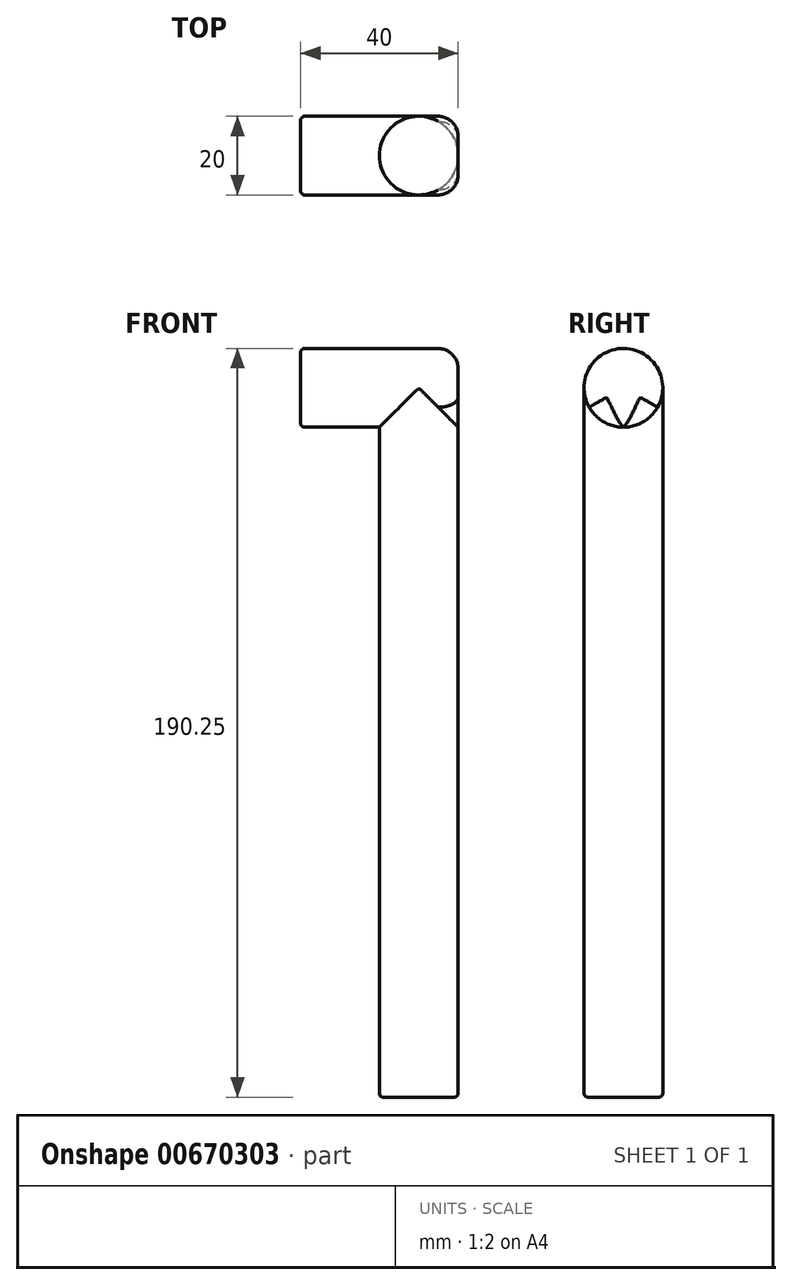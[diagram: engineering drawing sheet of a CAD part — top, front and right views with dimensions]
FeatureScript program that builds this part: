
annotation { "Feature Type Name" : "Feature", "Feature Type Description" : "" }
export const myFeature = defineFeature(function(context is Context, id is Id, definition is map)
    precondition{}
    {
        {
            var Q0;
            Q0=qCreatedBy(makeId("Top.planeOp"),FACE);
            var sketch = newSketch(context, id + "F0", { "sketchPlane" : qUnion([Q0])});
            skCircle(sketch, "E0", {"center": v(0, 0) * mm, "radius": 10 * mm});
            skSolve(sketch);
        }
        {
            var Q0;
            Q0=qCreatedBy(makeId("Right.planeOp"),FACE);
            cPlane(context, id + "F1", {"entities" : qUnion([Q0]), "cplaneType" : CPlaneType.OFFSET, "offset" : 30 * mm, "oppositeDirection" : true, "width" : 152.4 * mm, "height" : 152.4 * mm});
        }
        {
            var Q0;
            Q0=qCreatedBy(id+"F1.planeOp",FACE);
            var sketch = newSketch(context, id + "F2", { "sketchPlane" : qUnion([Q0])});
            skCircle(sketch, "E1", {"center": v(0, 180.25) * mm, "radius": 10 * mm});
            skLineSegment(sketch, "E2", {"start": v(0, 10.25) * mm, "end": v(0, 180.25) * mm});
            skSolve(sketch);
        }
        {
            var Q0;
            Q0 = qSketchRegion(id + "F0", true);
            extrude(context, id + "F3", {"entities" : qUnion([Q0]), "depth" : 180 * mm, "offsetDistance" : 25.4 * mm});
        }
        {
            var Q0;
            Q0 = qSketchRegion(id + "F2", true);
            extrude(context, id + "F4", {"entities" : qUnion([Q0]), "operationType" : NewBodyOperationType.ADD, "depth" : 40 * mm, "offsetDistance" : 25.4 * mm});
        }
        {
            var Q0;
            Q0=makeQuery(id+"F4.opExtrude","CAP_EDGE",EDGE,{"disambiguationData":[OSD([sQuery(id+"F2.wireOp",EDGE,"E1")])],"isStart":false});
            fillet(context, id + "F5", {"entities" : qUnion([Q0]), "radius" : 5.08 * mm, "tangentPropagation" : true, "allowEdgeOverflow" : false});
        }
        {
            var Q0;
            Q0=makeQuery(id+"F4.opExtrude","CAP_EDGE",EDGE,{"disambiguationData":[OSD([sQuery(id+"F2.wireOp",EDGE,"E1")])],"isStart":true});
            var Q1;
            Q1=makeQuery(id+"F3.opExtrude","CAP_EDGE",EDGE,{"disambiguationData":[OSD([sQuery(id+"F0.wireOp",EDGE,"E0")])],"isStart":true});
            fillet(context, id + "F6", {"entities" : qUnion([Q0, Q1]), "radius" : 1 * mm, "tangentPropagation" : true, "allowEdgeOverflow" : false});
        }
    });
